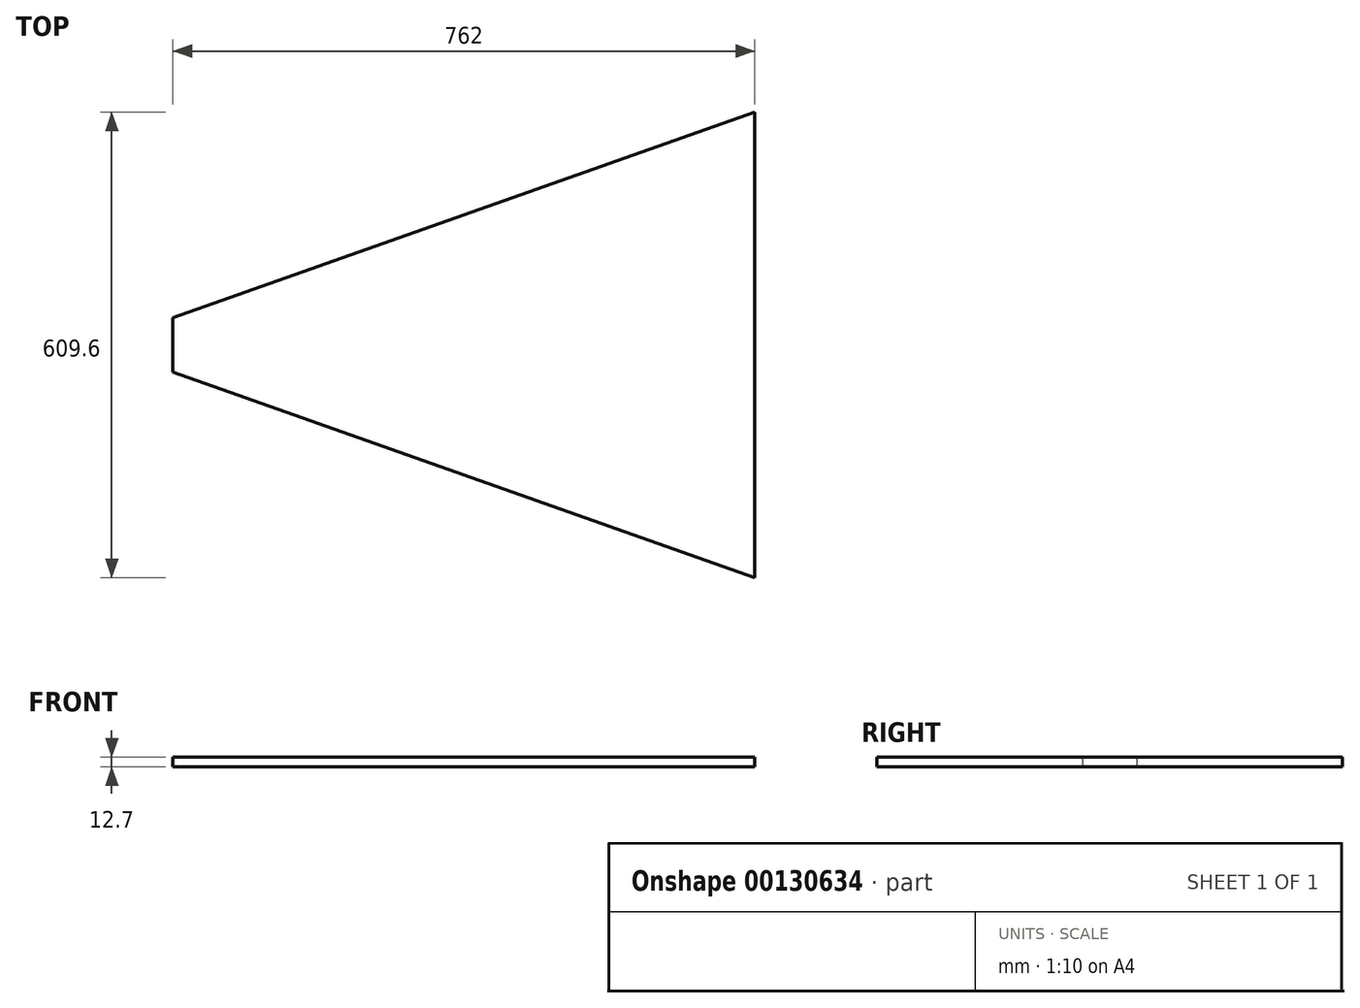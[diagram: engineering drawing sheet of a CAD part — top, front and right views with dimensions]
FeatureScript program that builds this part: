
annotation { "Feature Type Name" : "Feature", "Feature Type Description" : "" }
export const myFeature = defineFeature(function(context is Context, id is Id, definition is map)
    precondition{}
    {
        {
            var Q0;
            Q0=qCreatedBy(makeId("Top.planeOp"),FACE);
            var sketch = newSketch(context, id + "F0", { "sketchPlane" : qUnion([Q0])});
            skLineSegment(sketch, "E0.bottom", {"start": v(0, 0) * mm, "end": v(-78.38, 0) * mm});
            skLineSegment(sketch, "E0.top", {"start": v(0, 635) * mm, "end": v(-78.38, 635) * mm});
            skLineSegment(sketch, "E0.left", {"start": v(0, 0) * mm, "end": v(0, 635) * mm});
            skLineSegment(sketch, "E0.right", {"start": v(-114.3, 12.7) * mm, "end": v(-114.3, 622.3) * mm});
            skLineSegment(sketch, "E1", {"start": v(-114.3, 317.5) * mm, "end": v(-876.3, 317.5) * mm});
            skLineSegment(sketch, "E2", {"start": v(-78.38, 635) * mm, "end": v(-876.3, 352.9) * mm});
            skLineSegment(sketch, "E3", {"start": v(-78.38, 0) * mm, "end": v(-876.3, 282.1) * mm});
            skLineSegment(sketch, "E4", {"start": v(-876.3, 317.5) * mm, "end": v(-876.3, 352.9) * mm});
            skLineSegment(sketch, "E5", {"start": v(-876.3, 317.5) * mm, "end": v(-876.3, 282.1) * mm});
            skLineSegment(sketch, "E6", {"start": v(-876.3, 282.1) * mm, "end": v(-976.4, 317.5) * mm});
            skPoint(sketch, "E7.orphan", {"position": v(-114.3, 635) * mm});
            skPoint(sketch, "E8.end.orphan", {"position": v(-114.3, 12.7) * mm});
            skPoint(sketch, "E9.orphan", {"position": v(-114.3, 0) * mm});
            skSolve(sketch);
        }
        {
            var Q0;
            {var subQ0=sQuery(id+"F0.wireOp",EDGE,"E2");Q0=makeQuery(id+"F0.imprint","IMPRINT",FACE,{"disambiguationData":[TD([[makeQuery(id+"F0.imprint","IMPRINT",EDGE,{"derivedFrom":subQ0}),1.0]])]});}
            var Q1;
            {var subQ0=sQuery(id+"F0.wireOp",EDGE,"E3");Q1=makeQuery(id+"F0.imprint","IMPRINT",FACE,{"disambiguationData":[TD([[makeQuery(id+"F0.imprint","IMPRINT",EDGE,{"derivedFrom":subQ0}),-1.0]])]});}
            extrude(context, id + "F1", {"entities" : qUnion([Q0, Q1]), "depth" : 12.7 * mm});
        }
    });
